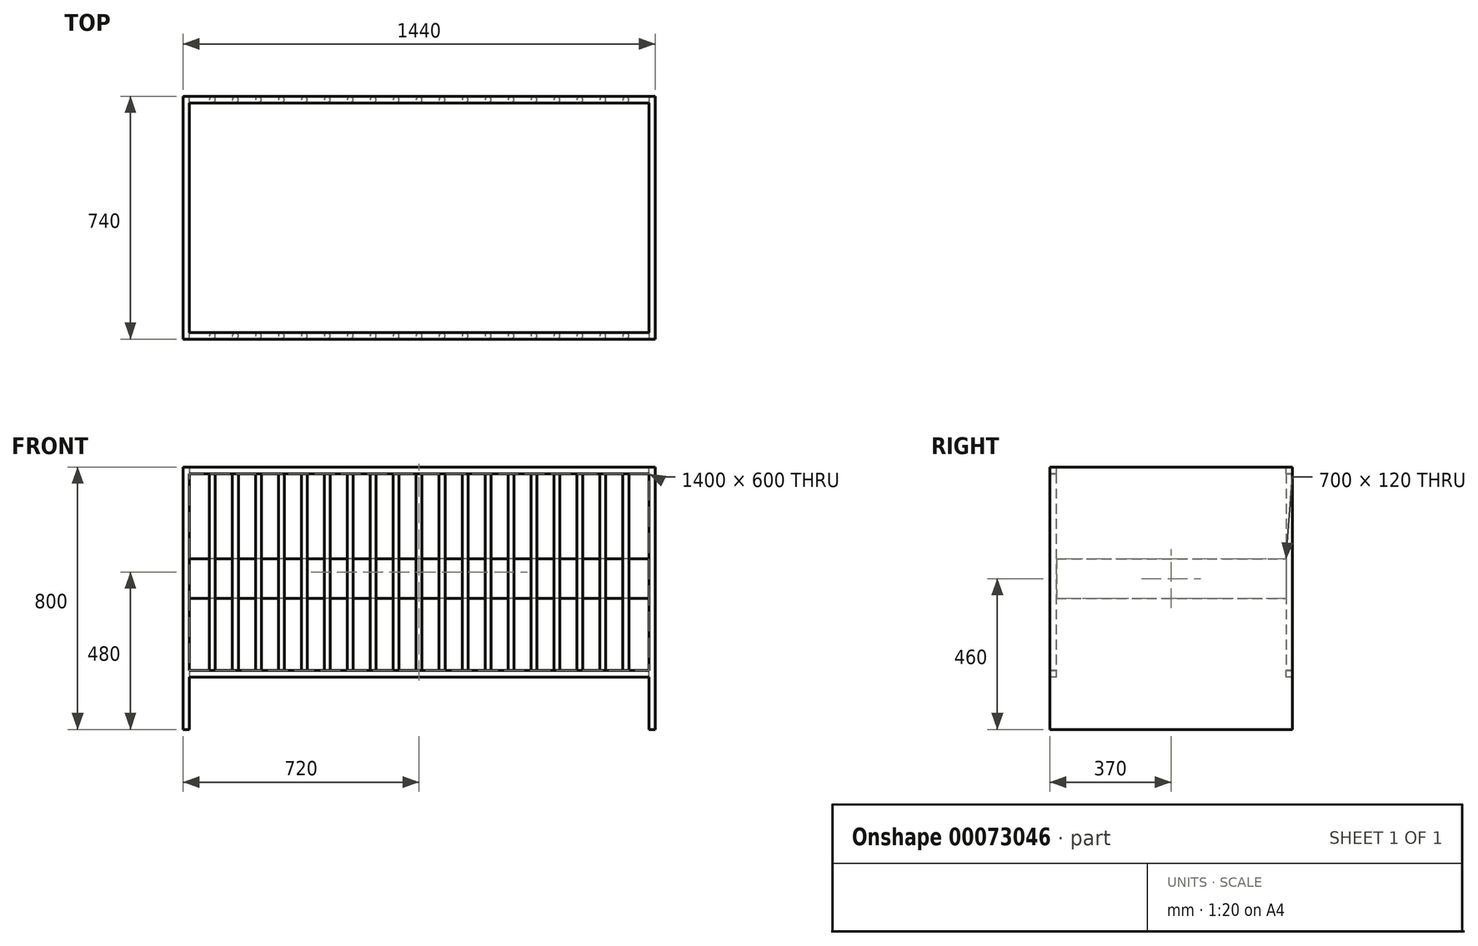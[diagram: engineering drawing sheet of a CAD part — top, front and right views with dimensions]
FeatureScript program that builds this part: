
annotation { "Feature Type Name" : "Feature", "Feature Type Description" : "" }
export const myFeature = defineFeature(function(context is Context, id is Id, definition is map)
    precondition{}
    {
        {
            var Q0;
            Q0=qCreatedBy(makeId("Top.planeOp"),FACE);
            var sketch = newSketch(context, id + "F0", { "sketchPlane" : qUnion([Q0])});
            skLineSegment(sketch, "E0.bottom", {"start": v(700, -350) * mm, "end": v(-700, -350) * mm});
            skLineSegment(sketch, "E0.top", {"start": v(700, 350) * mm, "end": v(-700, 350) * mm});
            skLineSegment(sketch, "E0.left", {"start": v(700, -350) * mm, "end": v(700, 350) * mm});
            skLineSegment(sketch, "E0.right", {"start": v(-700, -350) * mm, "end": v(-700, 350) * mm});
            skPoint(sketch, "E0.middle", {"position": v(0, 0) * mm});
            skLineSegment(sketch, "E1.0", {"start": v(-650, -300) * mm, "end": v(-650, 300) * mm});
            skLineSegment(sketch, "E1.1", {"start": v(650, -300) * mm, "end": v(-650, -300) * mm});
            skLineSegment(sketch, "E1.2", {"start": v(650, -300) * mm, "end": v(650, 300) * mm});
            skLineSegment(sketch, "E1.3", {"start": v(650, 300) * mm, "end": v(-650, 300) * mm});
            skSolve(sketch);
        }
        {
            var Q0;
            Q0=makeQuery(id+"F0.imprint","IMPRINT",FACE,{"disambiguationData":[TD([[makeQuery(id+"F0.imprint","IMPRINT",EDGE,{"derivedFrom":sQuery(id+"F0.wireOp",EDGE,"E0.bottom")}),-1.0]])]});
            extrude(context, id + "F1", {"entities" : qUnion([Q0]), "depth" : 25 * mm});
        }
        {
            var Q0;
            Q0=makeQuery(id+"F1.opExtrude","CAP_FACE",FACE,{"disambiguationData":[OSD([sQuery(id+"F0.wireOp",EDGE,"E0.bottom"),sQuery(id+"F0.wireOp",EDGE,"E0.top"),sQuery(id+"F0.wireOp",EDGE,"E0.left"),sQuery(id+"F0.wireOp",EDGE,"E0.right"),sQuery(id+"F0.wireOp",EDGE,"E1.0"),sQuery(id+"F0.wireOp",EDGE,"E1.1"),sQuery(id+"F0.wireOp",EDGE,"E1.2"),sQuery(id+"F0.wireOp",EDGE,"E1.3")])],"isStart":true});
            var sketch = newSketch(context, id + "F2", { "sketchPlane" : qUnion([Q0])});
            skLineSegment(sketch, "E2.bottom", {"start": v(-700, -370) * mm, "end": v(-720, -370) * mm});
            skLineSegment(sketch, "E2.top", {"start": v(-700, 370) * mm, "end": v(-720, 370) * mm});
            skLineSegment(sketch, "E2.left", {"start": v(-700, -370) * mm, "end": v(-700, 370) * mm});
            skLineSegment(sketch, "E2.right", {"start": v(-720, -370) * mm, "end": v(-720, 370) * mm});
            skPoint(sketch, "E2.middle", {"position": v(-710, 0) * mm});
            skLineSegment(sketch, "E3", {"start": v(0, 0) * mm, "end": v(0, 202.76) * mm, "construction": true});
            skLineSegment(sketch, "E4.MirrorCS", {"start": v(700, 370) * mm, "end": v(720, 370) * mm});
            skLineSegment(sketch, "E5.MirrorCS", {"start": v(700, -370) * mm, "end": v(720, -370) * mm});
            skLineSegment(sketch, "E6.MirrorCS", {"start": v(700, -370) * mm, "end": v(700, 370) * mm});
            skLineSegment(sketch, "E7.MirrorCS", {"start": v(720, -370) * mm, "end": v(720, 370) * mm});
            skPoint(sketch, "E8.MirrorP", {"position": v(710, 0) * mm});
            skSolve(sketch);
        }
        {
            var Q0;
            {var subQ3=sQuery(id+"F2.wireOp",EDGE,"E2.bottom");Q0=makeQuery(id+"F2.imprint","IMPRINT",FACE,{"disambiguationData":[TD([[makeQuery(id+"F2.imprint","IMPRINT",EDGE,{"derivedFrom":subQ3}),-1.0]])]});}
            var Q1;
            {var subQ4=sQuery(id+"F2.wireOp",EDGE,"E4.MirrorCS");Q1=makeQuery(id+"F2.imprint","IMPRINT",FACE,{"disambiguationData":[TD([[makeQuery(id+"F2.imprint","IMPRINT",EDGE,{"derivedFrom":subQ4}),-1.0]])]});}
            extrude(context, id + "F3", {"entities" : qUnion([Q0, Q1]), "operationType" : NewBodyOperationType.ADD, "depth" : 400 * mm, "hasSecondDirection" : true, "secondDirectionOppositeDirection" : true, "secondDirectionDepth" : 400 * mm});
        }
        {
            var Q0;
            Q0=makeQuery(id+"F3.opExtrude","SWEPT_FACE",FACE,{"disambiguationData":[OSD([sQuery(id+"F2.wireOp",EDGE,"E2.left")])]});
            var sketch = newSketch(context, id + "F4", { "sketchPlane" : qUnion([Q0])});
            skLineSegment(sketch, "E9.bottom", {"start": v(-370, 400) * mm, "end": v(-350, 400) * mm});
            skLineSegment(sketch, "E9.top", {"start": v(-370, 380) * mm, "end": v(-350, 380) * mm});
            skLineSegment(sketch, "E9.left", {"start": v(-370, 400) * mm, "end": v(-370, 380) * mm});
            skLineSegment(sketch, "E9.right", {"start": v(-350, 400) * mm, "end": v(-350, 380) * mm});
            skLineSegment(sketch, "E10.bottom", {"start": v(350, 400) * mm, "end": v(370, 400) * mm});
            skLineSegment(sketch, "E10.top", {"start": v(350, 380) * mm, "end": v(370, 380) * mm});
            skLineSegment(sketch, "E10.left", {"start": v(350, 400) * mm, "end": v(350, 380) * mm});
            skLineSegment(sketch, "E10.right", {"start": v(370, 400) * mm, "end": v(370, 380) * mm});
            skLineSegment(sketch, "E11.bottom", {"start": v(-370, -220) * mm, "end": v(-350, -220) * mm});
            skLineSegment(sketch, "E11.top", {"start": v(-370, -240) * mm, "end": v(-350, -240) * mm});
            skLineSegment(sketch, "E11.left", {"start": v(-370, -220) * mm, "end": v(-370, -240) * mm});
            skLineSegment(sketch, "E11.right", {"start": v(-350, -220) * mm, "end": v(-350, -240) * mm});
            skPoint(sketch, "E12.firstSnap0", {"position": v(-360, -220) * mm});
            skLineSegment(sketch, "E12.bottom", {"start": v(350, -220) * mm, "end": v(370, -220) * mm});
            skLineSegment(sketch, "E12.top", {"start": v(350, -240) * mm, "end": v(370, -240) * mm});
            skLineSegment(sketch, "E12.left", {"start": v(350, -220) * mm, "end": v(350, -240) * mm});
            skLineSegment(sketch, "E12.right", {"start": v(370, -220) * mm, "end": v(370, -240) * mm});
            skSolve(sketch);
        }
        {
            var Q0;
            Q0 = qSketchRegion(id + "F4", true);
            var Q1;
            Q1=makeQuery(id+"F3.opExtrude","SWEPT_FACE",FACE,{"disambiguationData":[OSD([sQuery(id+"F2.wireOp",EDGE,"E6.MirrorCS")])]});
            extrude(context, id + "F5", {"entities" : qUnion([Q0]), "operationType" : NewBodyOperationType.ADD, "endBound" : BoundingType.UP_TO_SURFACE, "endBoundEntityFace" : qUnion([Q1]), "depth" : 25 * mm});
        }
        {
            var Q0;
            Q0=makeQuery(id+"F5.opExtrude","SWEPT_FACE",FACE,{"disambiguationData":[OSD([sQuery(id+"F4.wireOp",EDGE,"E11.bottom")])]});
            var sketch = newSketch(context, id + "F6", { "sketchPlane" : qUnion([Q0])});
            skCircle(sketch, "E13", {"center": v(630, -360) * mm, "radius": 9 * mm});
            skCircle(sketch, "E14.1.0.0", {"center": v(560, -360) * mm, "radius": 9 * mm});
            skCircle(sketch, "E14.2.0.0", {"center": v(490, -360) * mm, "radius": 9 * mm});
            skLineSegment(sketch, "E14.direction1", {"start": v(630, -360) * mm, "end": v(560, -360) * mm, "construction": true});
            skCircle(sketch, "E15.0.3.0", {"center": v(420, -360) * mm, "radius": 9 * mm});
            skCircle(sketch, "E15.0.4.0", {"center": v(350, -360) * mm, "radius": 9 * mm});
            skCircle(sketch, "E15.0.5.0", {"center": v(280, -360) * mm, "radius": 9 * mm});
            skCircle(sketch, "E15.0.6.0", {"center": v(210, -360) * mm, "radius": 9 * mm});
            skCircle(sketch, "E15.0.7.0", {"center": v(140, -360) * mm, "radius": 9 * mm});
            skCircle(sketch, "E15.0.8.0", {"center": v(70, -360) * mm, "radius": 9 * mm});
            skCircle(sketch, "E15.0.9.0", {"center": v(0, -360) * mm, "radius": 9 * mm});
            skCircle(sketch, "E15.0.10.0", {"center": v(-70, -360) * mm, "radius": 9 * mm});
            skCircle(sketch, "E15.0.11.0", {"center": v(-140, -360) * mm, "radius": 9 * mm});
            skCircle(sketch, "E15.0.12.0", {"center": v(-210, -360) * mm, "radius": 9 * mm});
            skCircle(sketch, "E15.0.13.0", {"center": v(-280, -360) * mm, "radius": 9 * mm});
            skCircle(sketch, "E15.0.14.0", {"center": v(-350, -360) * mm, "radius": 9 * mm});
            skCircle(sketch, "E15.0.15.0", {"center": v(-420, -360) * mm, "radius": 9 * mm});
            skCircle(sketch, "E15.0.16.0", {"center": v(-490, -360) * mm, "radius": 9 * mm});
            skCircle(sketch, "E15.0.17.0", {"center": v(-560, -360) * mm, "radius": 9 * mm});
            skCircle(sketch, "E15.0.18.0", {"center": v(-630, -360) * mm, "radius": 9 * mm});
            skCircle(sketch, "E16.MirrorC", {"center": v(630, 360) * mm, "radius": 9 * mm});
            skCircle(sketch, "E17.MirrorC", {"center": v(560, 360) * mm, "radius": 9 * mm});
            skCircle(sketch, "E18.MirrorC", {"center": v(140, 360) * mm, "radius": 9 * mm});
            skCircle(sketch, "E19.MirrorC", {"center": v(70, 360) * mm, "radius": 9 * mm});
            skCircle(sketch, "E20.MirrorC", {"center": v(-420, 360) * mm, "radius": 9 * mm});
            skCircle(sketch, "E21.MirrorC", {"center": v(0, 360) * mm, "radius": 9 * mm});
            skCircle(sketch, "E22.MirrorC", {"center": v(-70, 360) * mm, "radius": 9 * mm});
            skCircle(sketch, "E23.MirrorC", {"center": v(-140, 360) * mm, "radius": 9 * mm});
            skCircle(sketch, "E24.MirrorC", {"center": v(-210, 360) * mm, "radius": 9 * mm});
            skCircle(sketch, "E25.MirrorC", {"center": v(-280, 360) * mm, "radius": 9 * mm});
            skCircle(sketch, "E26.MirrorC", {"center": v(-490, 360) * mm, "radius": 9 * mm});
            skCircle(sketch, "E27.MirrorC", {"center": v(-560, 360) * mm, "radius": 9 * mm});
            skCircle(sketch, "E28.MirrorC", {"center": v(-630, 360) * mm, "radius": 9 * mm});
            skCircle(sketch, "E29.MirrorC", {"center": v(-350, 360) * mm, "radius": 9 * mm});
            skCircle(sketch, "E30.MirrorC", {"center": v(490, 360) * mm, "radius": 9 * mm});
            skCircle(sketch, "E31.MirrorC", {"center": v(420, 360) * mm, "radius": 9 * mm});
            skCircle(sketch, "E32.MirrorC", {"center": v(350, 360) * mm, "radius": 9 * mm});
            skCircle(sketch, "E33.MirrorC", {"center": v(280, 360) * mm, "radius": 9 * mm});
            skCircle(sketch, "E34.MirrorC", {"center": v(210, 360) * mm, "radius": 9 * mm});
            skSolve(sketch);
        }
        {
            var Q0;
            Q0 = qSketchRegion(id + "F6", true);
            var Q1;
            Q1=makeQuery(id+"F5.opExtrude","SWEPT_FACE",FACE,{"disambiguationData":[OSD([sQuery(id+"F4.wireOp",EDGE,"E10.top")])]});
            extrude(context, id + "F7", {"entities" : qUnion([Q0]), "operationType" : NewBodyOperationType.ADD, "endBound" : BoundingType.UP_TO_SURFACE, "endBoundEntityFace" : qUnion([Q1]), "depth" : 300 * mm});
        }
        {
            var Q0;
            Q0=makeQuery(id+"F0.imprint","IMPRINT",FACE,{"disambiguationData":[TD([[makeQuery(id+"F0.imprint","IMPRINT",EDGE,{"derivedFrom":sQuery(id+"F0.wireOp",EDGE,"E1.0")}),-1.0]])]});
            extrude(context, id + "F8", {"entities" : qUnion([Q0]), "depth" : 120 * mm});
        }
        {
            var Q0;
            Q0=makeQuery(id+"F1.opExtrude","CAP_FACE",FACE,{"disambiguationData":[OSD([sQuery(id+"F0.wireOp",EDGE,"E0.bottom"),sQuery(id+"F0.wireOp",EDGE,"E0.top"),sQuery(id+"F0.wireOp",EDGE,"E0.left"),sQuery(id+"F0.wireOp",EDGE,"E0.right"),sQuery(id+"F0.wireOp",EDGE,"E1.0"),sQuery(id+"F0.wireOp",EDGE,"E1.1"),sQuery(id+"F0.wireOp",EDGE,"E1.2"),sQuery(id+"F0.wireOp",EDGE,"E1.3")])],"isStart":false});
            var Q1;
            Q1=makeQuery(id+"F8.opExtrude","CAP_FACE",FACE,{"disambiguationData":[OSD([sQuery(id+"F0.wireOp",EDGE,"E1.0"),sQuery(id+"F0.wireOp",EDGE,"E1.1"),sQuery(id+"F0.wireOp",EDGE,"E1.2"),sQuery(id+"F0.wireOp",EDGE,"E1.3")])],"isStart":false});
            extrude(context, id + "F9", {"entities" : qUnion([Q0]), "operationType" : NewBodyOperationType.ADD, "endBound" : BoundingType.UP_TO_SURFACE, "endBoundEntityFace" : qUnion([Q1]), "depth" : 25 * mm});
        }
    });
